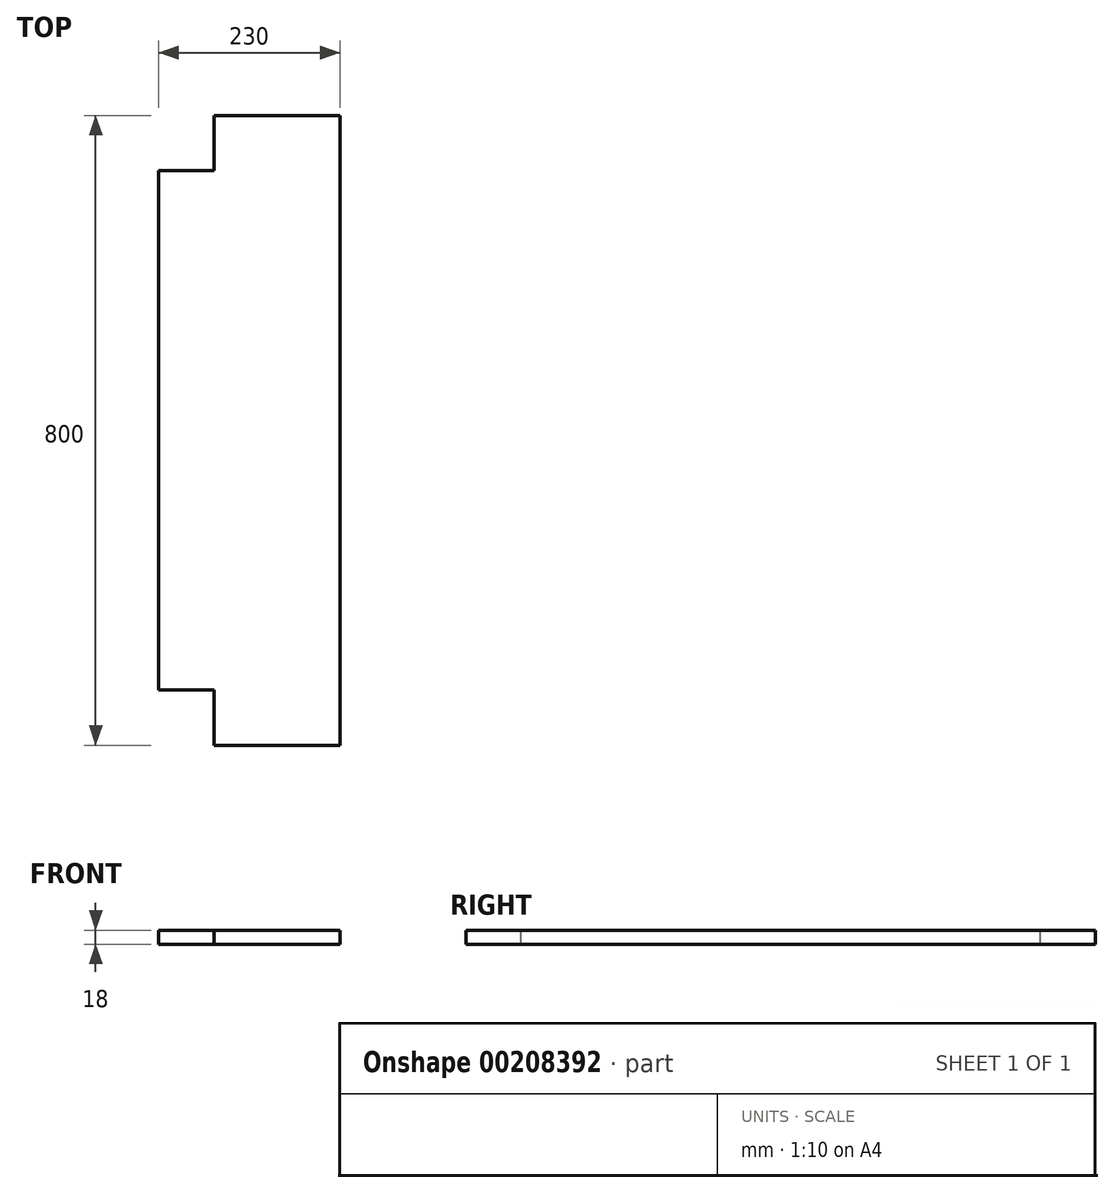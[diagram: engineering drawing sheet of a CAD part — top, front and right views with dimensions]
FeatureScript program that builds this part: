
annotation { "Feature Type Name" : "Feature", "Feature Type Description" : "" }
export const myFeature = defineFeature(function(context is Context, id is Id, definition is map)
    precondition{}
    {
        {
            var Q0;
            Q0=qCreatedBy(makeId("Front.planeOp"),FACE);
            var sketch = newSketch(context, id + "F0", { "sketchPlane" : qUnion([Q0])});
            skLineSegment(sketch, "E0.bottom", {"start": v(-34.1, 10.3) * mm, "end": v(195.9, 10.3) * mm});
            skLineSegment(sketch, "E0.top", {"start": v(-34.1, -7.7) * mm, "end": v(195.9, -7.7) * mm});
            skLineSegment(sketch, "E0.left", {"start": v(-34.1, 10.3) * mm, "end": v(-34.1, -7.7) * mm});
            skLineSegment(sketch, "E0.right", {"start": v(195.9, 10.3) * mm, "end": v(195.9, -7.7) * mm});
            skSolve(sketch);
        }
        {
            var Q0;
            Q0=makeQuery(id+"F0.imprint","IMPRINT",FACE,{"disambiguationData":[TD([[makeQuery(id+"F0.imprint","IMPRINT",EDGE,{"derivedFrom":sQuery(id+"F0.wireOp",EDGE,"E0.bottom")}),-1.0]])]});
            extrude(context, id + "F1", {"entities" : qUnion([Q0]), "oppositeDirection" : true, "depth" : 800 * mm});
        }
        {
            var Q0;
            Q0=makeQuery(id+"F1.opExtrude","SWEPT_FACE",FACE,{"disambiguationData":[OSD([sQuery(id+"F0.wireOp",EDGE,"E0.bottom")])]});
            var sketch = newSketch(context, id + "F2", { "sketchPlane" : qUnion([Q0])});
            skLineSegment(sketch, "E1.bottom", {"start": v(-34.1, 800) * mm, "end": v(35.9, 800) * mm});
            skLineSegment(sketch, "E1.top", {"start": v(-34.1, 730) * mm, "end": v(35.9, 730) * mm});
            skLineSegment(sketch, "E1.left", {"start": v(-34.1, 800) * mm, "end": v(-34.1, 730) * mm});
            skLineSegment(sketch, "E1.right", {"start": v(35.9, 800) * mm, "end": v(35.9, 730) * mm});
            skSolve(sketch);
        }
        {
            var Q0;
            Q0=makeQuery(id+"F2.imprint","IMPRINT",FACE,{"disambiguationData":[TD([[makeQuery(id+"F2.imprint","IMPRINT",EDGE,{"derivedFrom":sQuery(id+"F2.wireOp",EDGE,"E1.bottom")}),-1.0]])]});
            extrude(context, id + "F3", {"entities" : qUnion([Q0]), "operationType" : NewBodyOperationType.REMOVE, "oppositeDirection" : true, "depth" : 18 * mm});
        }
        {
            var Q0;
            Q0=makeQuery(id+"F1.opExtrude","SWEPT_FACE",FACE,{"disambiguationData":[OSD([sQuery(id+"F0.wireOp",EDGE,"E0.bottom")])]});
            var sketch = newSketch(context, id + "F4", { "sketchPlane" : qUnion([Q0])});
            skLineSegment(sketch, "E2.bottom", {"start": v(-34.1, 0) * mm, "end": v(35.9, 0) * mm});
            skLineSegment(sketch, "E2.top", {"start": v(-34.1, 70) * mm, "end": v(35.9, 70) * mm});
            skLineSegment(sketch, "E2.left", {"start": v(-34.1, 0) * mm, "end": v(-34.1, 70) * mm});
            skLineSegment(sketch, "E2.right", {"start": v(35.9, 0) * mm, "end": v(35.9, 70) * mm});
            skSolve(sketch);
        }
        {
            var Q0;
            Q0=makeQuery(id+"F4.imprint","IMPRINT",FACE,{"disambiguationData":[TD([[makeQuery(id+"F4.imprint","IMPRINT",EDGE,{"derivedFrom":sQuery(id+"F4.wireOp",EDGE,"E2.bottom")}),1.0]])]});
            extrude(context, id + "F5", {"entities" : qUnion([Q0]), "operationType" : NewBodyOperationType.REMOVE, "oppositeDirection" : true, "depth" : 18 * mm});
        }
    });
